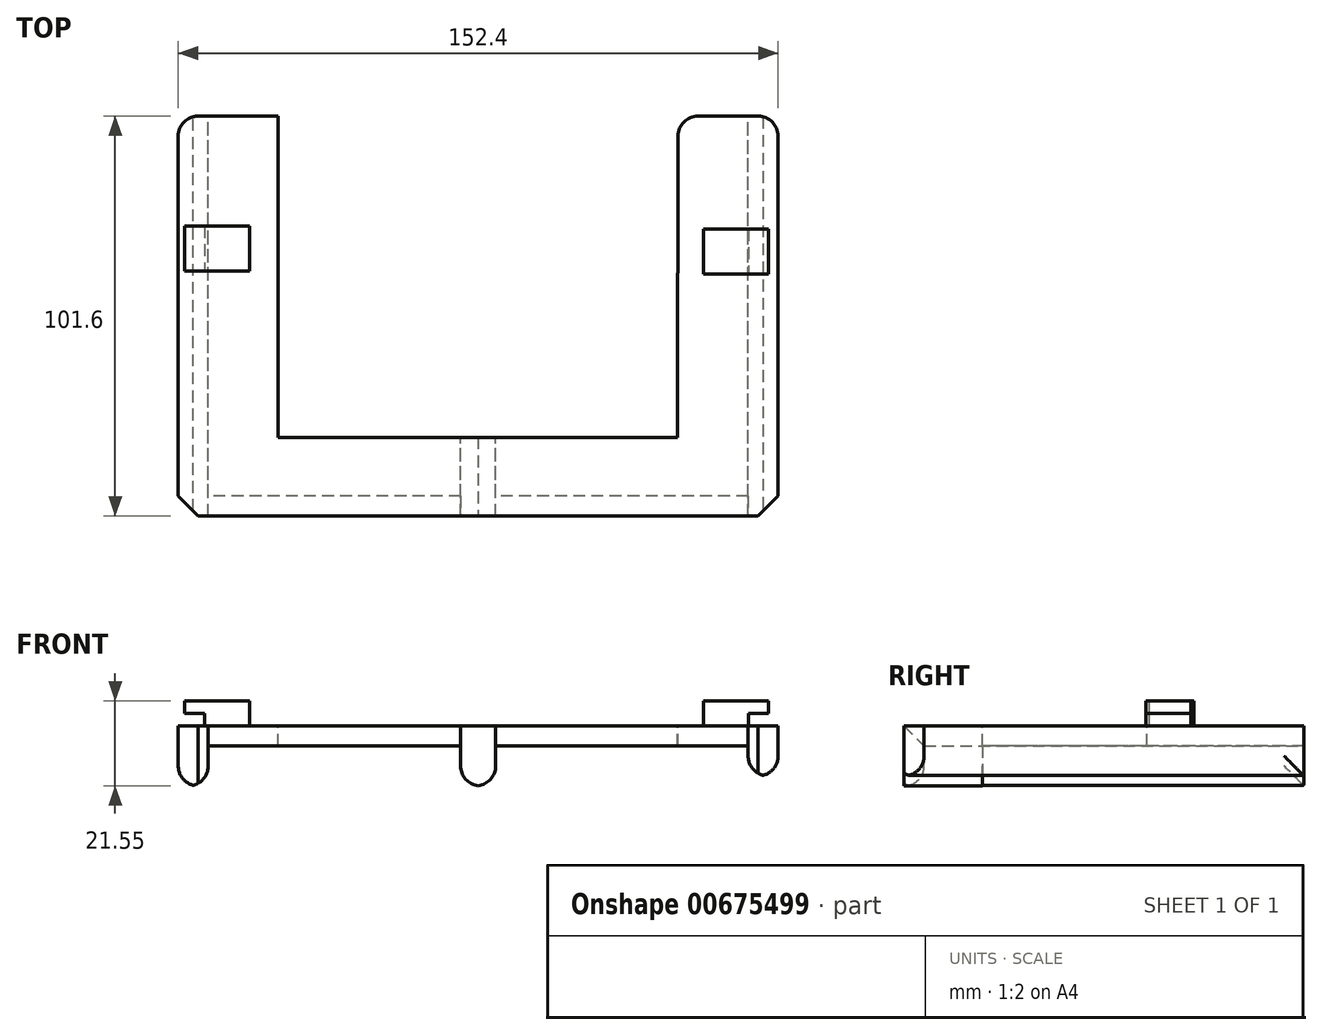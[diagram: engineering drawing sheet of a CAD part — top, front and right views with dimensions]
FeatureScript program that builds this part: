
annotation { "Feature Type Name" : "Feature", "Feature Type Description" : "" }
export const myFeature = defineFeature(function(context is Context, id is Id, definition is map)
    precondition{}
    {
        {
            var Q0;
            Q0=qCreatedBy(makeId("Top.planeOp"),FACE);
            var sketch = newSketch(context, id + "F0", { "sketchPlane" : qUnion([Q0])});
            skLineSegment(sketch, "E0.bottom", {"start": v(-76.2, 50.8) * mm, "end": v(76.2, 50.8) * mm});
            skLineSegment(sketch, "E0.top", {"start": v(-76.2, -50.8) * mm, "end": v(76.2, -50.8) * mm});
            skLineSegment(sketch, "E0.left", {"start": v(-76.2, 50.8) * mm, "end": v(-76.2, -50.8) * mm});
            skLineSegment(sketch, "E0.right", {"start": v(76.2, 50.8) * mm, "end": v(76.2, -50.8) * mm});
            skPoint(sketch, "E0.middle", {"position": v(0, 0) * mm});
            skSolve(sketch);
        }
        {
            var Q0;
            Q0 = qSketchRegion(id + "F0", true);
            extrude(context, id + "F1", {"entities" : qUnion([Q0]), "depth" : 5.08 * mm, "offsetDistance" : 25.4 * mm});
        }
        {
            var Q0;
            Q0=makeQuery(id+"F1.opExtrude","CAP_FACE",FACE,{"disambiguationData":[OSD([sQuery(id+"F0.wireOp",EDGE,"E0.bottom"),sQuery(id+"F0.wireOp",EDGE,"E0.top"),sQuery(id+"F0.wireOp",EDGE,"E0.left"),sQuery(id+"F0.wireOp",EDGE,"E0.right")])],"isStart":true});
            var sketch = newSketch(context, id + "F2", { "sketchPlane" : qUnion([Q0])});
            skLineSegment(sketch, "E1.bottom", {"start": v(-76.2, 50.8) * mm, "end": v(-68.58, 50.8) * mm});
            skLineSegment(sketch, "E1.top", {"start": v(-76.2, -50.8) * mm, "end": v(-68.58, -50.8) * mm});
            skLineSegment(sketch, "E1.left", {"start": v(-76.2, 50.8) * mm, "end": v(-76.2, -50.8) * mm});
            skLineSegment(sketch, "E1.right", {"start": v(-68.58, 50.8) * mm, "end": v(-68.58, -50.8) * mm});
            skSolve(sketch);
        }
        {
            var Q0;
            Q0 = qSketchRegion(id + "F2", true);
            extrude(context, id + "F3", {"entities" : qUnion([Q0]), "operationType" : NewBodyOperationType.ADD, "depth" : 10.16 * mm, "offsetDistance" : 25.4 * mm});
        }
        {
            var Q0;
            Q0=makeQuery(id+"F3.opExtrude","CAP_EDGE",EDGE,{"disambiguationData":[OSD([sQuery(id+"F2.wireOp",EDGE,"E1.left")])],"isStart":false});
            var Q1;
            Q1=makeQuery(id+"F3.opExtrude","CAP_EDGE",EDGE,{"disambiguationData":[OSD([sQuery(id+"F2.wireOp",EDGE,"E1.right")])],"isStart":false});
            fillet(context, id + "F4", {"entities" : qUnion([Q0, Q1]), "radius" : 5.08 * mm, "tangentPropagation" : true, "allowEdgeOverflow" : false});
        }
        {
            var Q0;
            Q0=makeQuery(id+"F1.opExtrude","CAP_FACE",FACE,{"disambiguationData":[OSD([sQuery(id+"F0.wireOp",EDGE,"E0.bottom"),sQuery(id+"F0.wireOp",EDGE,"E0.top"),sQuery(id+"F0.wireOp",EDGE,"E0.left"),sQuery(id+"F0.wireOp",EDGE,"E0.right")])],"isStart":true});
            var sketch = newSketch(context, id + "F5", { "sketchPlane" : qUnion([Q0])});
            skLineSegment(sketch, "E2.bottom", {"start": v(76.2, 50.8) * mm, "end": v(68.58, 50.8) * mm});
            skLineSegment(sketch, "E2.top", {"start": v(76.2, -50.8) * mm, "end": v(68.58, -50.8) * mm});
            skLineSegment(sketch, "E2.left", {"start": v(76.2, 50.8) * mm, "end": v(76.2, -50.8) * mm});
            skLineSegment(sketch, "E2.right", {"start": v(68.58, 50.8) * mm, "end": v(68.58, -50.8) * mm});
            skSolve(sketch);
        }
        {
            var Q0;
            Q0 = qSketchRegion(id + "F5", true);
            extrude(context, id + "F6", {"entities" : qUnion([Q0]), "operationType" : NewBodyOperationType.ADD, "depth" : 7.62 * mm, "offsetDistance" : 25.4 * mm});
        }
        {
            var Q0;
            Q0=makeQuery(id+"F6.opExtrude","CAP_EDGE",EDGE,{"disambiguationData":[OSD([sQuery(id+"F5.wireOp",EDGE,"E2.left")])],"isStart":false});
            var Q1;
            Q1=makeQuery(id+"F6.opExtrude","CAP_EDGE",EDGE,{"disambiguationData":[OSD([sQuery(id+"F5.wireOp",EDGE,"E2.right")])],"isStart":false});
            fillet(context, id + "F7", {"entities" : qUnion([Q0, Q1]), "radius" : 5.08 * mm, "tangentPropagation" : true, "allowEdgeOverflow" : false});
        }
        {
            var Q0;
            Q0=makeQuery(id+"F1.opExtrude","CAP_FACE",FACE,{"disambiguationData":[OSD([sQuery(id+"F0.wireOp",EDGE,"E0.bottom"),sQuery(id+"F0.wireOp",EDGE,"E0.top"),sQuery(id+"F0.wireOp",EDGE,"E0.left"),sQuery(id+"F0.wireOp",EDGE,"E0.right")])],"isStart":true});
            var sketch = newSketch(context, id + "F8", { "sketchPlane" : qUnion([Q0])});
            skLineSegment(sketch, "E3.bottom", {"start": v(-4.45, 50.8) * mm, "end": v(4.44, 50.8) * mm});
            skLineSegment(sketch, "E3.top", {"start": v(-4.45, -50.8) * mm, "end": v(4.44, -50.8) * mm});
            skLineSegment(sketch, "E3.left", {"start": v(-4.45, 50.8) * mm, "end": v(-4.45, -50.8) * mm});
            skLineSegment(sketch, "E3.right", {"start": v(4.44, 50.8) * mm, "end": v(4.44, -50.8) * mm});
            skSolve(sketch);
        }
        {
            var Q0;
            Q0 = qSketchRegion(id + "F8", true);
            extrude(context, id + "F9", {"entities" : qUnion([Q0]), "operationType" : NewBodyOperationType.ADD, "depth" : 10.16 * mm, "offsetDistance" : 25.4 * mm});
        }
        {
            var Q0;
            Q0=makeQuery(id+"F9.opExtrude","CAP_EDGE",EDGE,{"disambiguationData":[OSD([sQuery(id+"F8.wireOp",EDGE,"E3.left")])],"isStart":false});
            var Q1;
            Q1=makeQuery(id+"F9.opExtrude","CAP_EDGE",EDGE,{"disambiguationData":[OSD([sQuery(id+"F8.wireOp",EDGE,"E3.right")])],"isStart":false});
            fillet(context, id + "F10", {"entities" : qUnion([Q0, Q1]), "radius" : 5.08 * mm, "tangentPropagation" : true, "allowEdgeOverflow" : false});
        }
        {
            var Q0;
            Q0=makeQuery(id+"F1.opExtrude","CAP_FACE",FACE,{"disambiguationData":[OSD([sQuery(id+"F0.wireOp",EDGE,"E0.bottom"),sQuery(id+"F0.wireOp",EDGE,"E0.top"),sQuery(id+"F0.wireOp",EDGE,"E0.left"),sQuery(id+"F0.wireOp",EDGE,"E0.right")])],"isStart":false});
            var sketch = newSketch(context, id + "F11", { "sketchPlane" : qUnion([Q0])});
            skLineSegment(sketch, "E4.bottom", {"start": v(-50.8, 50.8) * mm, "end": v(50.8, 50.8) * mm});
            skLineSegment(sketch, "E4.top", {"start": v(-50.8, 6.85) * mm, "end": v(50.8, 6.85) * mm});
            skLineSegment(sketch, "E4.left", {"start": v(-50.8, 50.8) * mm, "end": v(-50.8, 6.85) * mm});
            skLineSegment(sketch, "E4.right", {"start": v(50.8, 50.8) * mm, "end": v(50.8, 6.85) * mm});
            skSolve(sketch);
        }
        {
            var Q0;
            Q0 = qSketchRegion(id + "F11", true);
            extrude(context, id + "F12", {"entities" : qUnion([Q0]), "operationType" : NewBodyOperationType.REMOVE, "oppositeDirection" : true, "depth" : 25.4 * mm, "offsetDistance" : 25.4 * mm});
        }
        {
            var Q0;
            Q0=makeQuery(id+"F12.boolean.opBoolean","COPY",EDGE,{"derivedFrom":makeQuery(id+"F12.opExtrude","SWEPT_EDGE",EDGE,{"disambiguationData":[OSD([sQuery(id+"F0.wireOp",EDGE,"E0.bottom"),sQuery(id+"F11.wireOp",EDGE,"E4.bottom"),sQuery(id+"F11.wireOp",EDGE,"E4.left")])]})});
            var Q1;
            Q1=makeQuery(id+"F12.boolean.opBoolean","COPY",EDGE,{"derivedFrom":makeQuery(id+"F12.opExtrude","SWEPT_EDGE",EDGE,{"disambiguationData":[OSD([sQuery(id+"F11.wireOp",EDGE,"E4.top"),sQuery(id+"F11.wireOp",EDGE,"E4.left")])]})});
            var Q2;
            Q2=makeQuery(id+"F12.boolean.opBoolean","COPY",EDGE,{"derivedFrom":makeQuery(id+"F12.opExtrude","SWEPT_EDGE",EDGE,{"disambiguationData":[OSD([sQuery(id+"F0.wireOp",EDGE,"E0.bottom"),sQuery(id+"F11.wireOp",EDGE,"E4.bottom"),sQuery(id+"F11.wireOp",EDGE,"E4.right")])]})});
            var Q3;
            Q3=makeQuery(id+"F12.boolean.opBoolean","COPY",EDGE,{"derivedFrom":makeQuery(id+"F12.opExtrude","SWEPT_EDGE",EDGE,{"disambiguationData":[OSD([sQuery(id+"F11.wireOp",EDGE,"E4.top"),sQuery(id+"F11.wireOp",EDGE,"E4.right")])]})});
            var Q4;
            Q4=makeQuery(id+"F3.boolean.opBoolean","MERGE",EDGE,{"derivedFrom":[makeQuery(id+"F1.opExtrude","SWEPT_EDGE",EDGE,{"disambiguationData":[OSD([sQuery(id+"F0.wireOp",EDGE,"E0.bottom"),sQuery(id+"F0.wireOp",EDGE,"E0.left")])]}),makeQuery(id+"F3.opExtrude","SWEPT_EDGE",EDGE,{"disambiguationData":[OSD([sQuery(id+"F2.wireOp",EDGE,"E1.top"),sQuery(id+"F2.wireOp",EDGE,"E1.left")])]})]});
            var Q5;
            Q5=makeQuery(id+"F6.boolean.opBoolean","MERGE",EDGE,{"derivedFrom":[makeQuery(id+"F1.opExtrude","SWEPT_EDGE",EDGE,{"disambiguationData":[OSD([sQuery(id+"F0.wireOp",EDGE,"E0.bottom"),sQuery(id+"F0.wireOp",EDGE,"E0.right")])]}),makeQuery(id+"F6.opExtrude","SWEPT_EDGE",EDGE,{"disambiguationData":[OSD([sQuery(id+"F5.wireOp",EDGE,"E2.top"),sQuery(id+"F5.wireOp",EDGE,"E2.left")])]})]});
            fillet(context, id + "F13", {"entities" : qUnion([Q0, Q1, Q2, Q3, Q4, Q5]), "radius" : 5.08 * mm, "tangentPropagation" : true, "allowEdgeOverflow" : false});
        }
        {
            var Q0;
            Q0=makeQuery(id+"F3.boolean.opBoolean","MERGE",EDGE,{"derivedFrom":[makeQuery(id+"F1.opExtrude","SWEPT_EDGE",EDGE,{"disambiguationData":[OSD([sQuery(id+"F0.wireOp",EDGE,"E0.top"),sQuery(id+"F0.wireOp",EDGE,"E0.left")])]}),makeQuery(id+"F3.opExtrude","SWEPT_EDGE",EDGE,{"disambiguationData":[OSD([sQuery(id+"F2.wireOp",EDGE,"E1.bottom"),sQuery(id+"F2.wireOp",EDGE,"E1.left")])]})]});
            var Q1;
            Q1=makeQuery(id+"F6.boolean.opBoolean","MERGE",EDGE,{"derivedFrom":[makeQuery(id+"F1.opExtrude","SWEPT_EDGE",EDGE,{"disambiguationData":[OSD([sQuery(id+"F0.wireOp",EDGE,"E0.top"),sQuery(id+"F0.wireOp",EDGE,"E0.right")])]}),makeQuery(id+"F6.opExtrude","SWEPT_EDGE",EDGE,{"disambiguationData":[OSD([sQuery(id+"F5.wireOp",EDGE,"E2.bottom"),sQuery(id+"F5.wireOp",EDGE,"E2.left")])]})]});
            var Q2;
            {var subQ0=sQuery(id+"F0.wireOp",EDGE,"E0.top");Q2=makeQuery(id+"F9.boolean.opBoolean","SPLIT",EDGE,{"disambiguationData":[TD([makeQuery(id+"F6.opExtrude","SWEPT_FACE",FACE,{"disambiguationData":[OSD([sQuery(id+"F5.wireOp",EDGE,"E2.right")])]})])],"derivedFrom":makeQuery(id+"F1.opExtrude","CAP_EDGE",EDGE,{"disambiguationData":[OSD([subQ0])],"isStart":true})});}
            var Q3;
            {var subQ0=sQuery(id+"F0.wireOp",EDGE,"E0.top");Q3=makeQuery(id+"F9.boolean.opBoolean","SPLIT",EDGE,{"disambiguationData":[TD([makeQuery(id+"F3.opExtrude","SWEPT_FACE",FACE,{"disambiguationData":[OSD([sQuery(id+"F2.wireOp",EDGE,"E1.right")])]})])],"derivedFrom":makeQuery(id+"F1.opExtrude","CAP_EDGE",EDGE,{"disambiguationData":[OSD([subQ0])],"isStart":true})});}
            chamfer(context, id + "F14", {"entities" : qUnion([Q0, Q1, Q2, Q3]), "width" : 5.08 * mm, "tangentPropagation" : true});
        }
        {
            var Q0;
            Q0=makeQuery(id+"F1.opExtrude","CAP_FACE",FACE,{"disambiguationData":[OSD([sQuery(id+"F0.wireOp",EDGE,"E0.bottom"),sQuery(id+"F0.wireOp",EDGE,"E0.top"),sQuery(id+"F0.wireOp",EDGE,"E0.left"),sQuery(id+"F0.wireOp",EDGE,"E0.right")])],"isStart":false});
            var sketch = newSketch(context, id + "F15", { "sketchPlane" : qUnion([Q0])});
            skLineSegment(sketch, "E5.bottom", {"start": v(68.73, 22.07) * mm, "end": v(57.3, 22.07) * mm});
            skLineSegment(sketch, "E5.top", {"start": v(68.73, 10.64) * mm, "end": v(57.3, 10.64) * mm});
            skLineSegment(sketch, "E5.left", {"start": v(68.73, 22.07) * mm, "end": v(68.73, 10.64) * mm});
            skLineSegment(sketch, "E5.right", {"start": v(57.3, 22.07) * mm, "end": v(57.3, 10.64) * mm});
            skSolve(sketch);
        }
        {
            var Q0;
            Q0 = qSketchRegion(id + "F15", true);
            extrude(context, id + "F16", {"entities" : qUnion([Q0]), "operationType" : NewBodyOperationType.ADD, "depth" : 6.35 * mm, "offsetDistance" : 25.4 * mm});
        }
        {
            var Q0;
            Q0=makeQuery(id+"F1.opExtrude","CAP_FACE",FACE,{"disambiguationData":[OSD([sQuery(id+"F0.wireOp",EDGE,"E0.bottom"),sQuery(id+"F0.wireOp",EDGE,"E0.top"),sQuery(id+"F0.wireOp",EDGE,"E0.left"),sQuery(id+"F0.wireOp",EDGE,"E0.right")])],"isStart":false});
            var sketch = newSketch(context, id + "F17", { "sketchPlane" : qUnion([Q0])});
            skLineSegment(sketch, "E6.bottom", {"start": v(-69.48, 22.85) * mm, "end": v(-58.05, 22.85) * mm});
            skLineSegment(sketch, "E6.top", {"start": v(-69.48, 11.42) * mm, "end": v(-58.05, 11.42) * mm});
            skLineSegment(sketch, "E6.left", {"start": v(-69.48, 22.85) * mm, "end": v(-69.48, 11.42) * mm});
            skLineSegment(sketch, "E6.right", {"start": v(-58.05, 22.85) * mm, "end": v(-58.05, 11.42) * mm});
            skSolve(sketch);
        }
        {
            var Q0;
            Q0 = qSketchRegion(id + "F17", true);
            extrude(context, id + "F18", {"entities" : qUnion([Q0]), "operationType" : NewBodyOperationType.ADD, "depth" : 6.35 * mm, "offsetDistance" : 25.4 * mm});
        }
        {
            var Q0;
            Q0=makeQuery(id+"F18.opExtrude","SWEPT_FACE",FACE,{"disambiguationData":[OSD([sQuery(id+"F17.wireOp",EDGE,"E6.left")])]});
            var sketch = newSketch(context, id + "F19", { "sketchPlane" : qUnion([Q0])});
            skLineSegment(sketch, "E7.bottom", {"start": v(-22.85, 11.43) * mm, "end": v(-11.42, 11.43) * mm});
            skLineSegment(sketch, "E7.top", {"start": v(-22.85, 8.26) * mm, "end": v(-11.42, 8.26) * mm});
            skLineSegment(sketch, "E7.left", {"start": v(-22.85, 11.43) * mm, "end": v(-22.85, 8.26) * mm});
            skLineSegment(sketch, "E7.right", {"start": v(-11.42, 11.43) * mm, "end": v(-11.42, 8.26) * mm});
            skSolve(sketch);
        }
        {
            var Q0;
            Q0 = qSketchRegion(id + "F19", true);
            extrude(context, id + "F20", {"entities" : qUnion([Q0]), "operationType" : NewBodyOperationType.ADD, "depth" : 5.08 * mm, "offsetDistance" : 25.4 * mm});
        }
        {
            var Q0;
            Q0=makeQuery(id+"F16.opExtrude","SWEPT_FACE",FACE,{"disambiguationData":[OSD([sQuery(id+"F15.wireOp",EDGE,"E5.left")])]});
            var sketch = newSketch(context, id + "F21", { "sketchPlane" : qUnion([Q0])});
            skLineSegment(sketch, "E8.bottom", {"start": v(10.64, 11.43) * mm, "end": v(22.07, 11.43) * mm});
            skLineSegment(sketch, "E8.top", {"start": v(10.64, 8.26) * mm, "end": v(22.07, 8.26) * mm});
            skLineSegment(sketch, "E8.left", {"start": v(10.64, 11.43) * mm, "end": v(10.64, 8.26) * mm});
            skLineSegment(sketch, "E8.right", {"start": v(22.07, 11.43) * mm, "end": v(22.07, 8.26) * mm});
            skSolve(sketch);
        }
        {
            var Q0;
            Q0 = qSketchRegion(id + "F21", true);
            extrude(context, id + "F22", {"entities" : qUnion([Q0]), "operationType" : NewBodyOperationType.ADD, "depth" : 5.08 * mm, "offsetDistance" : 25.4 * mm});
        }
        {
            var Q0;
            Q0=makeQuery(id+"F1.opExtrude","CAP_FACE",FACE,{"disambiguationData":[OSD([sQuery(id+"F0.wireOp",EDGE,"E0.bottom"),sQuery(id+"F0.wireOp",EDGE,"E0.top"),sQuery(id+"F0.wireOp",EDGE,"E0.left"),sQuery(id+"F0.wireOp",EDGE,"E0.right")])],"isStart":false});
            var sketch = newSketch(context, id + "F23", { "sketchPlane" : qUnion([Q0])});
            skLineSegment(sketch, "E9.bottom", {"start": v(-50.8, 11.93) * mm, "end": v(50.68, 11.93) * mm});
            skLineSegment(sketch, "E9.top", {"start": v(-50.8, -30.83) * mm, "end": v(50.68, -30.83) * mm});
            skLineSegment(sketch, "E9.left", {"start": v(-50.8, 11.93) * mm, "end": v(-50.8, -30.83) * mm});
            skLineSegment(sketch, "E9.right", {"start": v(50.68, 11.93) * mm, "end": v(50.68, -30.83) * mm});
            skSolve(sketch);
        }
        {
            var Q0;
            Q0 = qSketchRegion(id + "F23", true);
            extrude(context, id + "F24", {"entities" : qUnion([Q0]), "operationType" : NewBodyOperationType.REMOVE, "oppositeDirection" : true, "depth" : 25.4 * mm, "offsetDistance" : 25.4 * mm});
        }
    });
